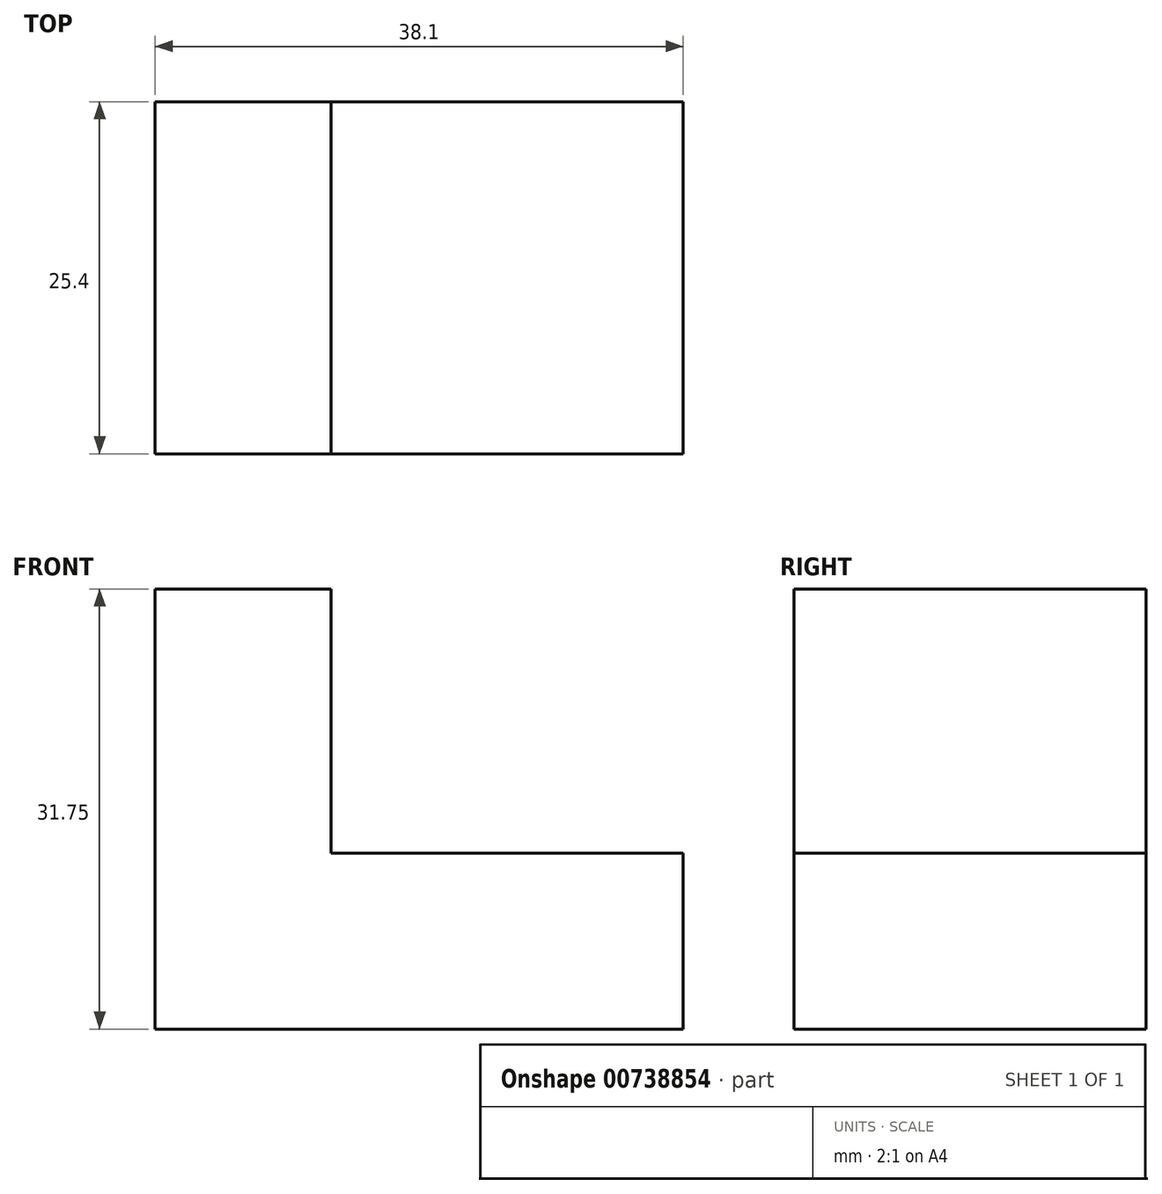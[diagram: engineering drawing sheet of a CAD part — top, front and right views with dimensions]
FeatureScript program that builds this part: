
annotation { "Feature Type Name" : "Feature", "Feature Type Description" : "" }
export const myFeature = defineFeature(function(context is Context, id is Id, definition is map)
    precondition{}
    {
        {
            var Q0;
            Q0=qCreatedBy(makeId("Front.planeOp"),FACE);
            var sketch = newSketch(context, id + "F0", { "sketchPlane" : qUnion([Q0])});
            skLineSegment(sketch, "E0", {"start": v(0, 31.75) * mm, "end": v(0, -0.99) * mm});
            skLineSegment(sketch, "E1", {"start": v(0, 31.75) * mm, "end": v(0, 0) * mm});
            skLineSegment(sketch, "E2", {"start": v(0, 0) * mm, "end": v(38.1, 0) * mm});
            skLineSegment(sketch, "E3", {"start": v(38.1, 12.7) * mm, "end": v(12.7, 12.7) * mm});
            skLineSegment(sketch, "E4", {"start": v(12.7, 12.7) * mm, "end": v(12.7, 31.75) * mm});
            skLineSegment(sketch, "E5", {"start": v(12.7, 31.75) * mm, "end": v(0, 31.75) * mm});
            skLineSegment(sketch, "E6", {"start": v(38.1, 12.7) * mm, "end": v(38.1, 0) * mm});
            skLineSegment(sketch, "E7", {"start": v(38.1, 0) * mm, "end": v(38.1, 12.7) * mm});
            skSolve(sketch);
        }
        {
            var Q0;
            Q0 = qSketchRegion(id + "F0", true);
            extrude(context, id + "F1", {"entities" : qUnion([Q0]), "depth" : 25.4 * mm, "offsetDistance" : 25.4 * mm});
        }
    });
